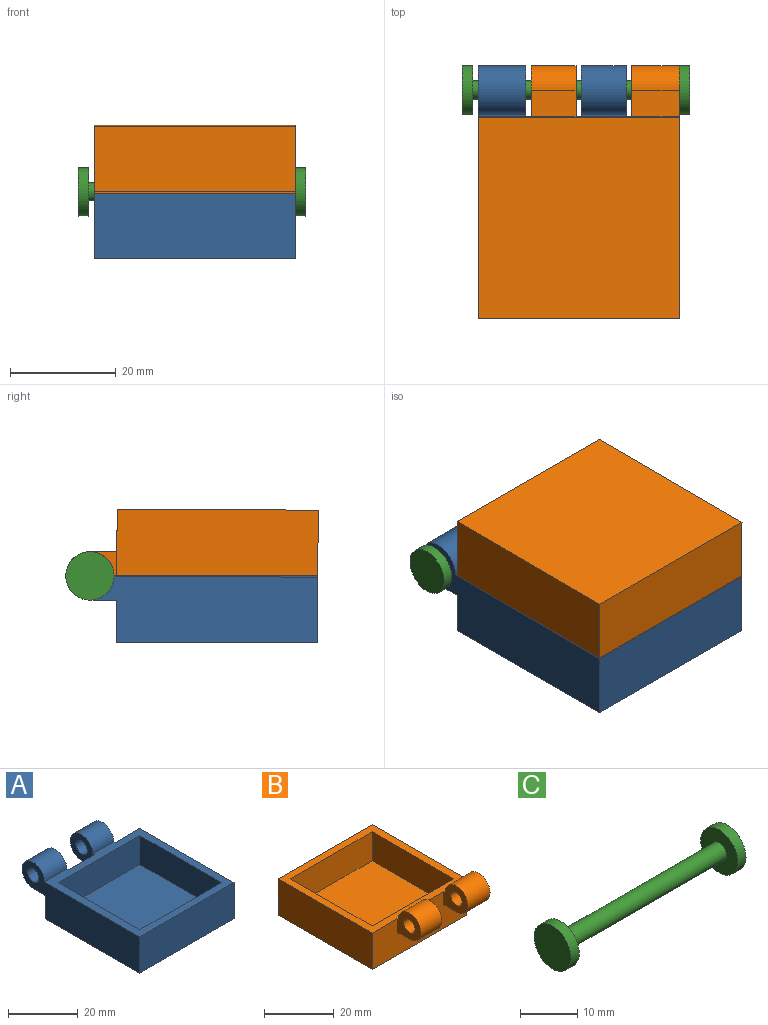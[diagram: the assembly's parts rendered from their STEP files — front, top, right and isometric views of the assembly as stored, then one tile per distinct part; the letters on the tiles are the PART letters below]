
ASSEMBLY  parts=3 mates=4
PART A: 20 faces, bbox 38.1x47.8x17.3 mm
  f0: plane 38.1x12.7mm, normal (1,0,0), area 483.9mm2, adj f1,f4,f6,f7
  f1: plane 38.61x38.1mm, normal (0,0,1), area 370.2mm2, adj f0,f2,f4,f5,f6,f8,f9,f10
  f2: cylinder r=4.57mm len=9.14mm, axis (-1,0,0), area 183.3mm2, adj f1,f3,f16,f17
  f3: plane 8.51x5.08mm, normal (0,0,-1), area 43.2mm2, adj f2,f4,f16,f17
  f4: plane 38.1x12.7mm, normal (0,1,0), area 403.7mm2, adj f0,f1,f3,f5,f7,f14,f16,f17
  f5: plane 47.75x17.27mm, normal (-1,0,0), area 539.9mm2, adj f1,f4,f6,f7,f13,f14,f15
  f6: plane 38.1x12.7mm, normal (0,-1,0), area 483.9mm2, adj f0,f1,f5,f7
  f7: plane 38.1x38.1mm, normal (0,0,-1), area 1451.6mm2, adj f0,f4,f5,f6
  f8: plane 33.02x10.16mm, normal (-1,0,0), area 335.5mm2, adj f1,f9,f11,f12
  f9: plane 33.02x10.16mm, normal (0,-1,0), area 335.5mm2, adj f1,f8,f10,f12
  f10: plane 33.02x10.16mm, normal (1,0,0), area 335.5mm2, adj f1,f9,f11,f12
  f11: plane 33.02x10.16mm, normal (0,1,0), area 335.5mm2, adj f1,f8,f10,f12
  f12: plane 33.02x33.02mm, normal (0,0,1), area 1090.3mm2, adj f8,f9,f10,f11
  f13: cylinder r=4.57mm len=9.14mm, axis (-1,0,0), area 194.3mm2, adj f1,f5,f14,f18
  f14: plane 9.02x5.08mm, normal (0,0,-1), area 45.8mm2, adj f4,f5,f13,f18
  f15: cylinder r=2.29mm len=9.02mm, axis (-1,0,0), area 129.5mm2, adj f5,f18
  f16: plane 9.65x9.14mm, normal (1,0,0), area 56.1mm2, adj f1,f2,f3,f4,f19
  f17: plane 9.65x9.14mm, normal (-1,0,0), area 56.1mm2, adj f1,f2,f3,f4,f19
  f18: plane 9.65x9.14mm, normal (1,0,0), area 56.1mm2, adj f1,f4,f13,f14,f15
  f19: cylinder r=2.29mm len=8.51mm, axis (-1,0,0), area 122.2mm2, adj f16,f17
PART B: 20 faces, bbox 38.1x47.8x17.3 mm
  f0: plane 38.1x12.7mm, normal (-1,0,0), area 483.9mm2, adj f1,f4,f6,f7
  f1: plane 38.61x38.1mm, normal (0,0,1), area 370.2mm2, adj f0,f2,f4,f5,f6,f8,f9,f10
  f2: cylinder r=4.57mm len=9.14mm, axis (1,0,0), area 183.3mm2, adj f1,f3,f16,f17
  f3: plane 8.51x5.08mm, normal (0,0,-1), area 43.2mm2, adj f2,f4,f16,f17
  f4: plane 38.1x12.7mm, normal (0,-1,0), area 403.7mm2, adj f0,f1,f3,f5,f7,f14,f16,f17
  f5: plane 47.75x17.27mm, normal (1,0,0), area 539.9mm2, adj f1,f4,f6,f7,f13,f14,f15
  f6: plane 38.1x12.7mm, normal (0,1,0), area 483.9mm2, adj f0,f1,f5,f7
  f7: plane 38.1x38.1mm, normal (0,0,-1), area 1451.6mm2, adj f0,f4,f5,f6
  f8: plane 33.02x10.16mm, normal (1,0,0), area 335.5mm2, adj f1,f9,f11,f12
  f9: plane 33.02x10.16mm, normal (0,1,0), area 335.5mm2, adj f1,f8,f10,f12
  f10: plane 33.02x10.16mm, normal (-1,0,0), area 335.5mm2, adj f1,f9,f11,f12
  f11: plane 33.02x10.16mm, normal (0,-1,0), area 335.5mm2, adj f1,f8,f10,f12
  f12: plane 33.02x33.02mm, normal (0,0,1), area 1090.3mm2, adj f8,f9,f10,f11
  f13: cylinder r=4.57mm len=9.14mm, axis (1,0,0), area 194.3mm2, adj f1,f5,f14,f18
  f14: plane 9.02x5.08mm, normal (0,0,-1), area 45.8mm2, adj f4,f5,f13,f18
  f15: cylinder r=2.29mm len=9.02mm, axis (1,0,0), area 129.5mm2, adj f5,f18
  f16: plane 9.65x9.14mm, normal (-1,0,0), area 56.1mm2, adj f1,f2,f3,f4,f19
  f17: plane 9.65x9.14mm, normal (1,0,0), area 56.1mm2, adj f1,f2,f3,f4,f19
  f18: plane 9.65x9.14mm, normal (-1,0,0), area 56.1mm2, adj f1,f4,f13,f14,f15
  f19: cylinder r=2.29mm len=8.51mm, axis (1,0,0), area 122.2mm2, adj f16,f17
PART C: 7 faces, bbox 43.2x9.1x9.1 mm
  f0: cylinder r=1.78mm len=39.12mm, axis (-1,0,0), area 437mm2, adj f1,f4
  f1: plane 9.14x9.14mm, normal (-1,0,0), area 55.7mm2, adj f0,f3
  f2: plane 9.14x9.14mm, normal (1,0,0), area 65.7mm2, adj f3
  f3: cylinder r=4.57mm len=9.14mm, axis (-1,0,0), area 58.4mm2, adj f1,f2
  f4: plane 9.14x9.14mm, normal (1,0,0), area 55.7mm2, adj f0,f5
  f5: cylinder r=4.57mm len=9.14mm, axis (-1,0,0), area 58.4mm2, adj f4,f6
  f6: plane 9.14x9.14mm, normal (-1,0,0), area 65.7mm2, adj f5
PLACE A at identity fixed
PLACE B rot(axis=(-1,0,0),179.7deg) t=(0,48.19,25.54)mm
PLACE C t=(-0.51,0,0)mm
MATE planar A.f0 <-> B.f5  axis (1,0,0) through (19.05,0,6.35)mm
MATE cylindrical C.f0 <-> A.f2  axis (-1,0,0) through (-0.51,24.13,12.7)mm
MATE cylindrical C.f0 <-> B.f2  axis (-1,0,0) through (-0.51,24.13,12.7)mm
MATE planar C.f3 <-> B.f5  axis (-1,0,0) through (19.05,24.13,12.7)mm
